# Revit family: Construction_Roof-Accessories_Alpine-SnowGuards_ASG2000B-Mini
name_source: partatom
category: Specialty Equipment
units: mm (PartAtom-declared; Revit-internal decimal feet)

## family parameters
Cut with Voids When Loaded = No
Host = Face
OmniClass Number = 23.35.20.31.27.14
OmniClass Title = Snow Guards
Part Type = Normal
Room Calculation Point = No
Round Connector Dimension = Use Diameter
Shared = No

## types (1)
- Two Pipe
    Assembly Code = B3010
    Default Elevation = 48"
    Description = ASG2000B-Mini two-rod, pipe-style bracket in brass.
    Edition number = 1
    Horizontal Spacing = 10"
    Keynote = 07720
    Manufacturer = Alpine SnowGuards
    Model = ASG2000B-MINI
    Pad Material = Alpine SnowGuards - Brass - Mill Finish
    Product Guid = 0acb7519-8dd1-4c52-b7b6-b8f9a123a0dc
    Product Material = Alpine SnowGuards - Brass - Mill Finish
    Product data url = https://www.bimobject.com
    URL = https://www.alpinesnowguards.com

## geometry (parser evidence)
native form markers: Sweep x9
no freeform markers — native parametric forms only
